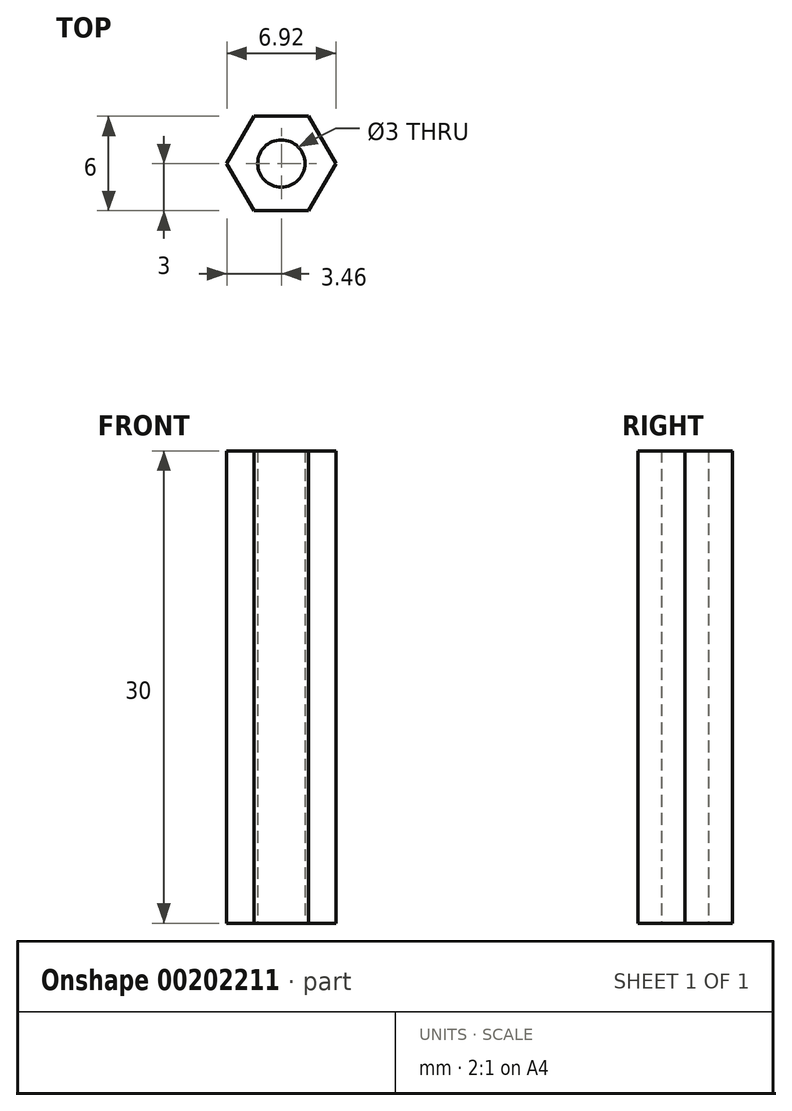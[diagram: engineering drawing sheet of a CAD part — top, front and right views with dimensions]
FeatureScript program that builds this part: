
annotation { "Feature Type Name" : "Feature", "Feature Type Description" : "" }
export const myFeature = defineFeature(function(context is Context, id is Id, definition is map)
    precondition{}
    {
        {
            var Q0;
            Q0=qCreatedBy(makeId("Top.planeOp"),FACE);
            var sketch = newSketch(context, id + "F0", { "sketchPlane" : qUnion([Q0])});
            skCircle(sketch, "E0.cCircle", {"center": v(0, 0) * mm, "radius": 3 * mm, "construction": true});
            skLineSegment(sketch, "E0.0", {"start": v(-1.73, 3) * mm, "end": v(1.73, 3) * mm});
            skLineSegment(sketch, "E0.1", {"start": v(1.73, 3) * mm, "end": v(3.46, 0) * mm});
            skLineSegment(sketch, "E0.2", {"start": v(3.46, 0) * mm, "end": v(1.73, -3) * mm});
            skLineSegment(sketch, "E0.3", {"start": v(1.73, -3) * mm, "end": v(-1.73, -3) * mm});
            skLineSegment(sketch, "E0.4", {"start": v(-1.73, -3) * mm, "end": v(-3.46, 0) * mm});
            skLineSegment(sketch, "E0.5", {"start": v(-3.46, 0) * mm, "end": v(-1.73, 3) * mm});
            skPoint(sketch, "E0.0.midPoint", {"position": v(0, 3) * mm});
            skCircle(sketch, "E1", {"center": v(0, 0) * mm, "radius": 1.5 * mm});
            skSolve(sketch);
        }
        {
            var Q0;
            Q0=qSketchRegion(id+"F0",true);
            extrude(context, id + "F1", {"entities" : qUnion([Q0]), "depth" : 30 * mm});
        }
    });
